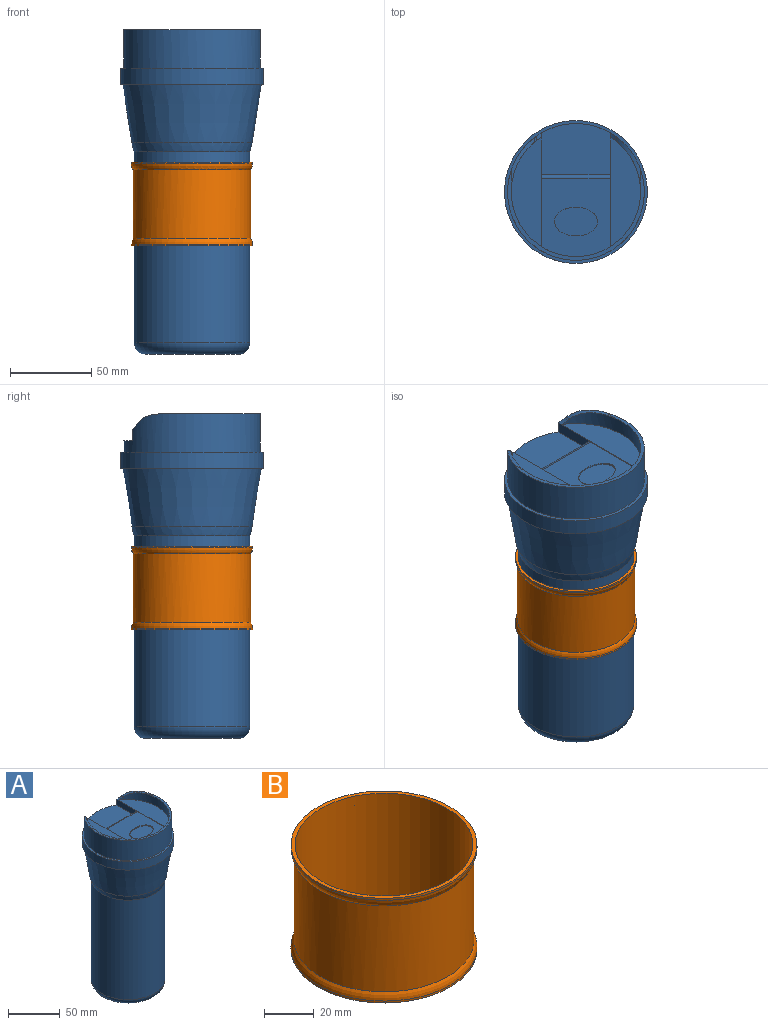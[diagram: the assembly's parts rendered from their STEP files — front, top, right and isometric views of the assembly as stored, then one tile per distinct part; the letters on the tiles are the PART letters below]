
ASSEMBLY  parts=2 mates=1
PART A: 28 faces, bbox 92.2x146.6x199.5 mm
  f0: plane 70.12x6.92mm, normal (1,0,0), area 205.8mm2, adj f7,f8,f11,f12,f14,f18,f22,f25
  f1: plane 87.76x87.76mm, normal (0,0,1), area 513.8mm2, adj f5,f7
  f2: cylinder r=35.56mm len=117.35mm, axis (0,0,-1), area 26222.6mm2, adj f15,f16
  f3: plane 56.64x56.64mm, normal (0,0,-1), area 2520mm2, adj f16
  f4: cone r=42.56mm half-angle=9deg, axis (0,0,1), area 8925.6mm2, adj f15,f23
  f5: cylinder r=43.88mm len=87.76mm, axis (0,0,-1), area 2726.7mm2, adj f1,f6
  f6: plane 87.76x87.76mm, normal (0,0,-1), area 357.1mm2, adj f5,f23
  f7: cylinder r=41.98mm len=83.95mm, axis (0,0,-1), area 5363.9mm2, adj f0,f1,f8,f9,f19,f20,f21,f24
  f8: plane 41.98x31.48mm, normal (0,0,1), area 1245mm2, adj f0,f7,f9,f12
  f9: plane 70.12x6.92mm, normal (-1,0,0), area 205.8mm2, adj f7,f8,f10,f12,f14,f18,f22,f24
  f10: plane 67.5x18.76mm, normal (0,0,1), area 894.2mm2, adj f9,f18
  f11: plane 67.5x18.76mm, normal (0,0,1), area 894.2mm2, adj f0,f18
  f12: plane 41.98x4.3mm, normal (0,1,0), area 180.5mm2, adj f0,f8,f9,f22
  f13: extruded ~26.42x17.59mm, area 62.8mm2, adj f14,f17
  f14: plane 48.24x41.98mm, normal (0,0,1), area 1578.7mm2, adj f0,f9,f13,f18,f22
  f15: torus R=2.52mm, axis (0,0,-1), area 1341.8mm2, adj f2,f4
  f16: torus R=28.32mm, axis (0,0,1), area 2354.1mm2, adj f2,f3
  f17: plane 26.42x17.59mm, normal (0,0,1), area 365mm2, adj f13
  f18: cylinder r=39.75mm len=79.49mm, axis (0,0,-1), area 1856.6mm2, adj f0,f9,f10,f11,f14,f19,f20,f21
  f19: plane 83.95x55.94mm, normal (0,0,1), area 331.6mm2, adj f7,f18,f26,f27
  f20: plane 3.51x1.07mm, normal (0.71,0.01,0.71), area 3.9mm2, adj f7,f18,f25,f26
  f21: plane 3.51x1.07mm, normal (-0.71,0.01,0.71), area 3.9mm2, adj f7,f18,f24,f27
  f22: cylinder r=2mm len=41.98mm, axis (1,0,0), area 131.9mm2, adj f0,f9,f12,f14
  f23: torus R=39.31mm, axis (0,0,1), area 85.3mm2, adj f4,f6
  f24: bspline ~97.17x5.48mm, area 11.3mm2, adj f7,f9,f18,f21
  f25: bspline ~4.82x3.39mm, area 11.3mm2, adj f0,f7,f18,f20
  f26: cylinder r=20.63mm len=28.75mm, axis (-0.01,1,0), area 64.9mm2, adj f7,f18,f19,f20
  f27: cylinder r=20.63mm len=28.75mm, axis (-0.01,-1,0), area 64.9mm2, adj f7,f18,f19,f21
PART B: 8 faces, bbox 80.6x80.6x51.3 mm
  f0: cylinder r=35.57mm len=71.14mm, axis (0,0,-1), area 11458.5mm2, adj f2,f5
  f1: cylinder r=37.23mm len=74.47mm, axis (0,0,-1), area 220.3mm2, adj f2,f7
  f2: plane 74.47x74.47mm, normal (0,0,-1), area 380.8mm2, adj f0,f1
  f3: cylinder r=36mm len=72mm, axis (0,0,-1), area 9516mm2, adj f6,f7
  f4: cylinder r=37.23mm len=74.47mm, axis (0,0,-1), area 220.3mm2, adj f5,f6
  f5: plane 74.47x74.47mm, normal (0,0,1), area 380.8mm2, adj f0,f4
  f6: torus R=31.2mm, axis (0,0,-1), area 909.2mm2, adj f3,f4
  f7: torus R=31.2mm, axis (0,0,1), area 909.2mm2, adj f1,f3
PLACE A t=(-40.12,1.5,-63.95)mm
PLACE B t=(-40.12,1.5,2.71)mm
MATE fastened B.f0 <-> A.f2  axis (0,0,-1) through (-40.12,1.5,28.35)mm
